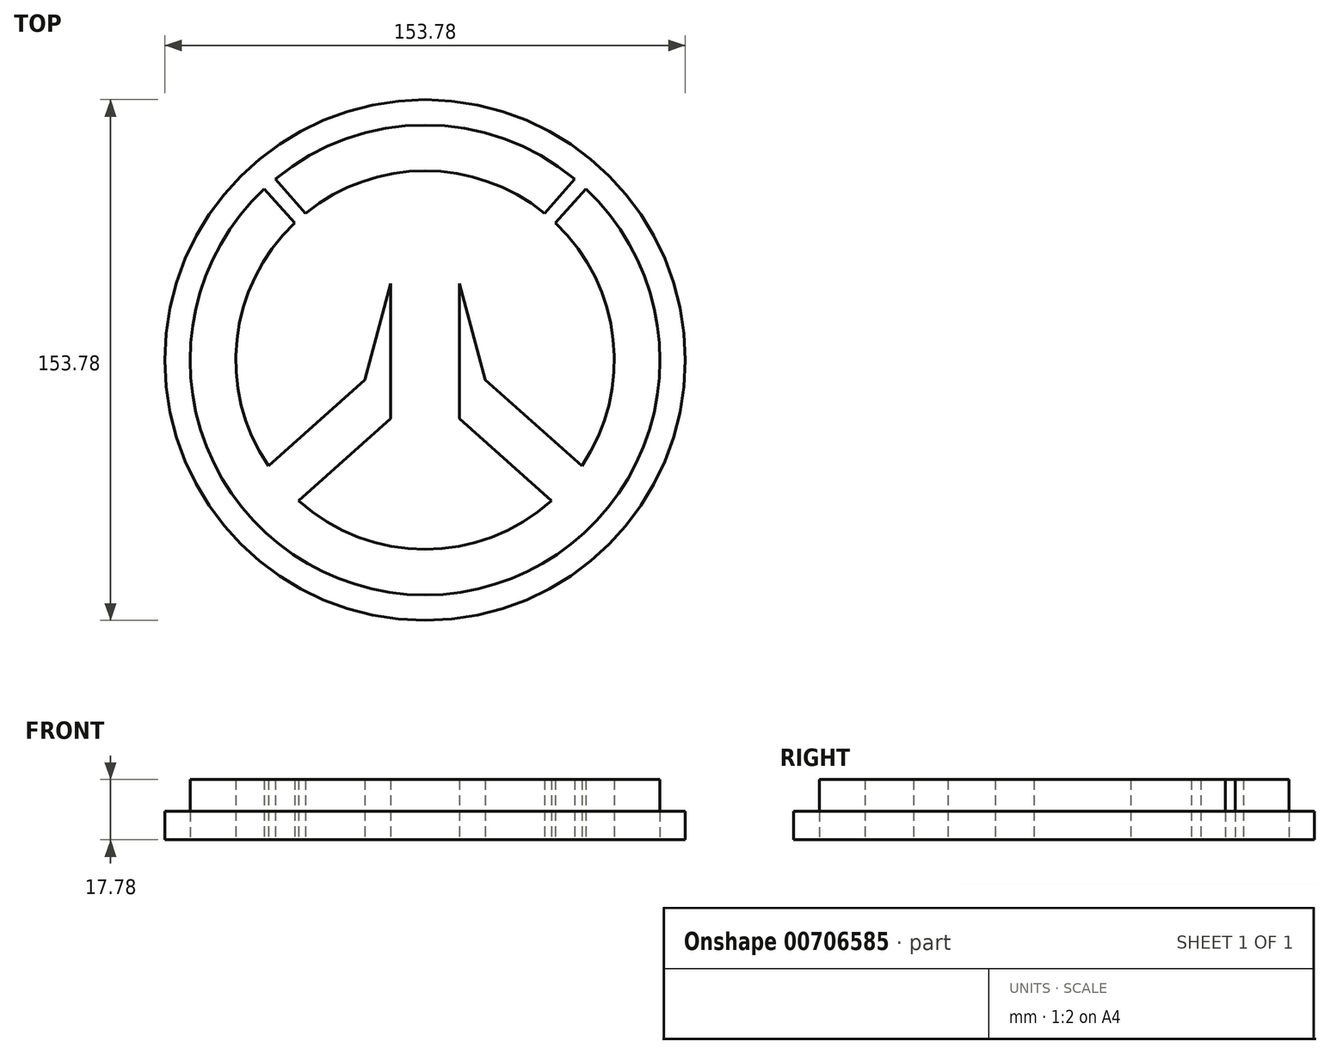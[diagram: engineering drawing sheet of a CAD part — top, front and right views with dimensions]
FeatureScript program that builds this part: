
annotation { "Feature Type Name" : "Feature", "Feature Type Description" : "" }
export const myFeature = defineFeature(function(context is Context, id is Id, definition is map)
    precondition{}
    {
        {
            var Q0;
            Q0=qCreatedBy(makeId("Top.planeOp"),FACE);
            var sketch = newSketch(context, id + "F0", { "sketchPlane" : qUnion([Q0])});
            skArc(sketch, "E0", {"start": v(-47.5, 50.57) * mm, "mid": v(0, -69.38) * mm, "end": v(47.5, 50.57) * mm});
            skArc(sketch, "E1", {"start": v(-38.52, 40.48) * mm, "mid": v(-55.55, 6.01) * mm, "end": v(-46.29, -31.3) * mm});
            skLineSegment(sketch, "E2", {"start": v(-35.25, 43.35) * mm, "end": v(-44.22, 53.46) * mm});
            skLineSegment(sketch, "E3", {"start": v(-47.5, 50.57) * mm, "end": v(-38.52, 40.48) * mm});
            skLineSegment(sketch, "E4.MirrorCS", {"start": v(35.25, 43.35) * mm, "end": v(44.22, 53.46) * mm});
            skLineSegment(sketch, "E5.MirrorCS", {"start": v(47.5, 50.57) * mm, "end": v(38.52, 40.48) * mm});
            skArc(sketch, "E6.trimOffspring", {"start": v(44.22, 53.46) * mm, "mid": v(0, 69.38) * mm, "end": v(-44.22, 53.46) * mm});
            skArc(sketch, "E7.trimOffspring", {"start": v(35.25, 43.35) * mm, "mid": v(0, 55.88) * mm, "end": v(-35.25, 43.35) * mm});
            skLineSegment(sketch, "E8", {"start": v(-46.29, -31.3) * mm, "end": v(-17.74, -5.91) * mm});
            skLineSegment(sketch, "E9", {"start": v(-10.17, -17.34) * mm, "end": v(-37.37, -41.54) * mm});
            skArc(sketch, "E10.trimOffspring", {"start": v(-37.37, -41.54) * mm, "mid": v(0, -55.88) * mm, "end": v(37.37, -41.54) * mm});
            skLineSegment(sketch, "E11", {"start": v(-17.74, -5.91) * mm, "end": v(-10.17, 22.63) * mm});
            skLineSegment(sketch, "E12", {"start": v(-10.17, -17.34) * mm, "end": v(-10.17, 22.63) * mm});
            skLineSegment(sketch, "E13.MirrorCS", {"start": v(10.17, -17.34) * mm, "end": v(10.17, 22.63) * mm});
            skLineSegment(sketch, "E14.MirrorCS", {"start": v(17.74, -5.91) * mm, "end": v(10.17, 22.63) * mm});
            skLineSegment(sketch, "E15.MirrorCS", {"start": v(46.29, -31.3) * mm, "end": v(17.74, -5.91) * mm});
            skLineSegment(sketch, "E16.MirrorCS", {"start": v(10.17, -17.34) * mm, "end": v(37.37, -41.54) * mm});
            skArc(sketch, "E17.trimOffspring", {"start": v(46.29, -31.3) * mm, "mid": v(55.55, 6.01) * mm, "end": v(38.52, 40.48) * mm});
            skSolve(sketch);
        }
        {
            var Q0;
            Q0=makeQuery(id+"F0.imprint","IMPRINT",FACE,{"disambiguationData":[TD([[makeQuery(id+"F0.imprint","IMPRINT",EDGE,{"derivedFrom":sQuery(id+"F0.wireOp",EDGE,"E2")}),-1.0]])]});
            var Q1;
            Q1=makeQuery(id+"F0.imprint","IMPRINT",FACE,{"disambiguationData":[TD([[makeQuery(id+"F0.imprint","IMPRINT",EDGE,{"derivedFrom":sQuery(id+"F0.wireOp",EDGE,"E0")}),1.0]])]});
            extrude(context, id + "F1", {"entities" : qUnion([Q0, Q1]), "depth" : 17.78 * mm, "offsetDistance" : 25.4 * mm});
        }
        {
            var Q0;
            Q0=qCreatedBy(makeId("Top.planeOp"),FACE);
            var sketch = newSketch(context, id + "F2", { "sketchPlane" : qUnion([Q0])});
            skCircle(sketch, "E18", {"center": v(0, 0) * mm, "radius": 76.89 * mm});
            skSolve(sketch);
        }
        {
            var Q0;
            Q0=makeQuery(id+"F2.imprint","IMPRINT",FACE,{"disambiguationData":[TD([[makeQuery(id+"F2.imprint","IMPRINT",EDGE,{"derivedFrom":sQuery(id+"F2.wireOp",EDGE,"E18")}),1.0]])]});
            extrude(context, id + "F3", {"entities" : qUnion([Q0]), "depth" : 8.38 * mm, "offsetDistance" : 25.4 * mm});
        }
    });
